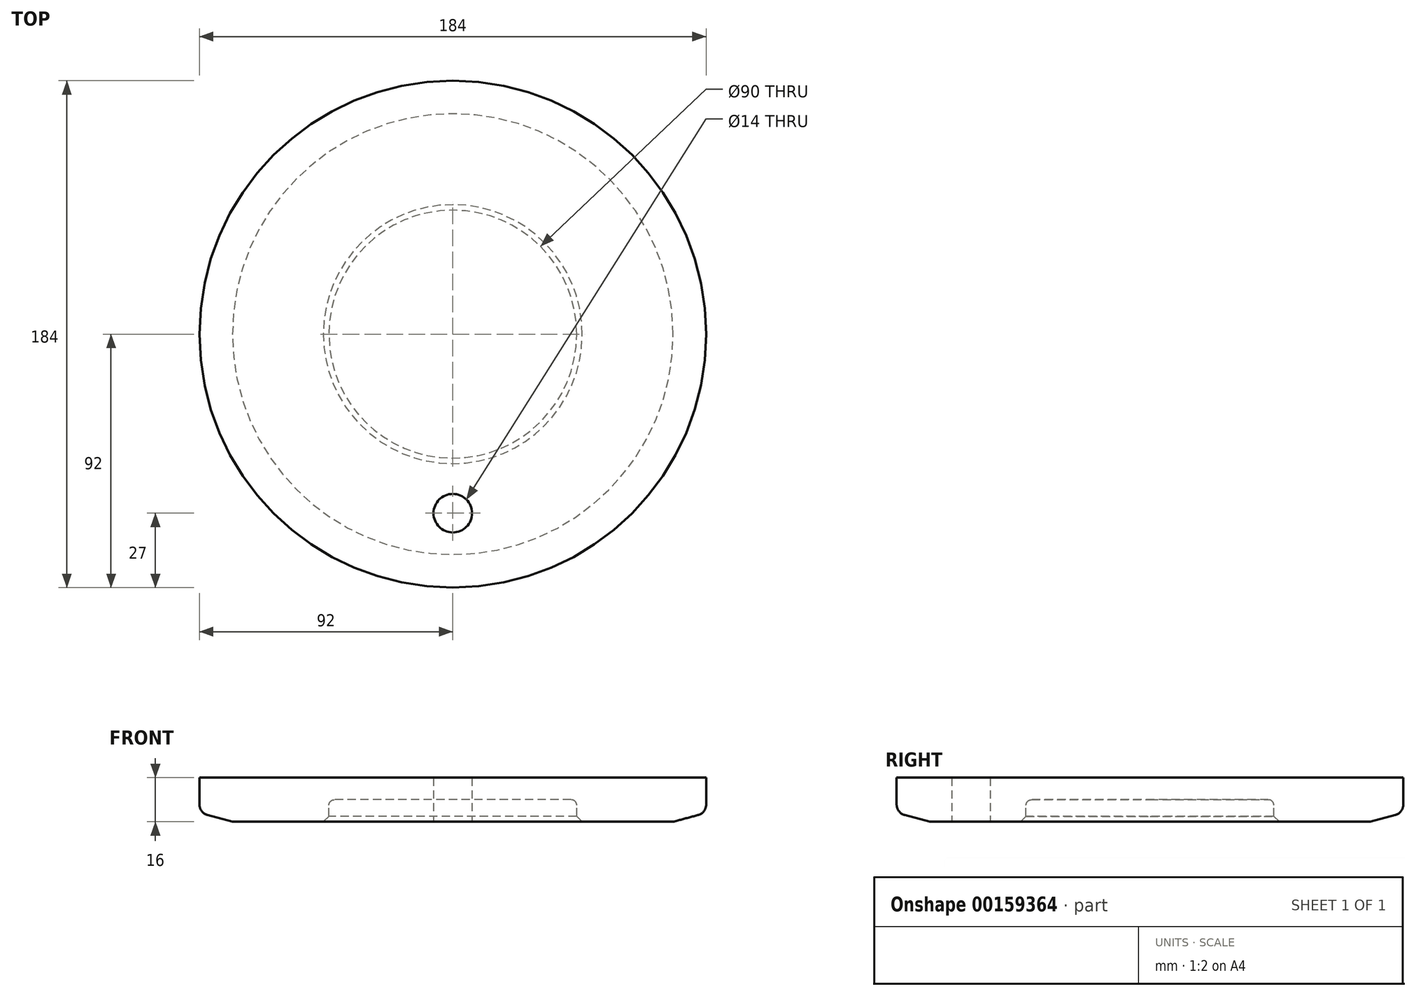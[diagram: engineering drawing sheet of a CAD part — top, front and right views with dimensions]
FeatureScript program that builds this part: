
annotation { "Feature Type Name" : "Feature", "Feature Type Description" : "" }
export const myFeature = defineFeature(function(context is Context, id is Id, definition is map)
    precondition{}
    {
        {
            var Q0;
            Q0=qCreatedBy(makeId("Right.planeOp"),FACE);
            var sketch = newSketch(context, id + "F0", { "sketchPlane" : qUnion([Q0])});
            skLineSegment(sketch, "E0", {"start": v(-50.07, 0) * mm, "end": v(57.08, 0) * mm, "construction": true});
            skLineSegment(sketch, "E1", {"start": v(0, 48.61) * mm, "end": v(0, -46.86) * mm, "construction": true});
            skLineSegment(sketch, "E2.bottom", {"start": v(0, 16) * mm, "end": v(92, 16) * mm});
            skLineSegment(sketch, "E2.top", {"start": v(45, 0) * mm, "end": v(80, 0) * mm});
            skLineSegment(sketch, "E2.left", {"start": v(0, 16) * mm, "end": v(0, 0) * mm});
            skLineSegment(sketch, "E2.right", {"start": v(92, 16) * mm, "end": v(92, 6.28) * mm});
            skPoint(sketch, "E3", {"position": v(80, 0) * mm});
            skLineSegment(sketch, "E4", {"start": v(80, 0) * mm, "end": v(89.04, 2.42) * mm});
            skPoint(sketch, "E5.visualSharp", {"position": v(92, 3.22) * mm});
            skArc(sketch, "E5.filletArc", {"start": v(89.04, 2.42) * mm, "mid": v(91.17, 3.85) * mm, "end": v(92, 6.28) * mm});
            skPoint(sketch, "E6", {"position": v(45, 0) * mm});
            skLineSegment(sketch, "E7.top", {"start": v(43, 8) * mm, "end": v(0, 8) * mm});
            skLineSegment(sketch, "E7.left", {"start": v(45, 0) * mm, "end": v(45, 6) * mm});
            skPoint(sketch, "E8.visualSharp", {"position": v(45, 8) * mm});
            skArc(sketch, "E8.filletArc", {"start": v(45, 6) * mm, "mid": v(44.41, 7.41) * mm, "end": v(43, 8) * mm});
            skSolve(sketch);
        }
        {
            var Q0;
            {var subQ1=sQuery(id+"F0.wireOp",EDGE,"E2.bottom");Q0=makeQuery(id+"F0.imprint","IMPRINT",FACE,{"disambiguationData":[TD([[makeQuery(id+"F0.imprint","IMPRINT",EDGE,{"derivedFrom":subQ1}),-1.0]])]});}
            var Q1;
            Q1=sQuery(id+"F0.wireOp",EDGE,"E1");
            revolve(context, id + "F1", {"entities" : qUnion([Q0]), "axis" : qUnion([Q1]), "revolveType" : RevolveType.FULL});
        }
        {
            var Q0;
            Q0=makeQuery(id+"F1.opRevolve","SWEPT_EDGE",EDGE,{"disambiguationData":[OSD([sQuery(id+"F0.wireOp",EDGE,"E2.top"),sQuery(id+"F0.wireOp",EDGE,"E7.left")])]});
            chamfer(context, id + "F2", {"entities" : qUnion([Q0]), "chamferType" : ChamferType.OFFSET_ANGLE, "width" : 2 * mm, "oppositeDirection" : false, "angle" : 45 * degree, "tangentPropagation" : true});
        }
        {
            var Q0;
            Q0=makeQuery(id+"F1.opRevolve","SWEPT_FACE",FACE,{"disambiguationData":[OSD([sQuery(id+"F0.wireOp",EDGE,"E2.top")])]});
            var sketch = newSketch(context, id + "F3", { "sketchPlane" : qUnion([Q0])});
            skCircle(sketch, "E9", {"center": v(0, 0) * mm, "radius": 65 * mm, "construction": true});
            skPoint(sketch, "E10", {"position": v(0, 65) * mm});
            skCircle(sketch, "E11", {"center": v(0, 65) * mm, "radius": 7 * mm});
            skSolve(sketch);
        }
        {
            var Q0;
            Q0=makeQuery(id+"F3.imprint","IMPRINT",FACE,{"disambiguationData":[TD([[makeQuery(id+"F3.imprint","IMPRINT",EDGE,{"derivedFrom":sQuery(id+"F3.wireOp",EDGE,"E11")}),1.0]])]});
            extrude(context, id + "F4", {"entities" : qUnion([Q0]), "operationType" : NewBodyOperationType.REMOVE, "oppositeDirection" : true, "depth" : 25 * mm});
        }
        {
            var Q0;
            Q0=qCreatedBy(makeId("Front.planeOp"),FACE);
            var sketch = newSketch(context, id + "F5", { "sketchPlane" : qUnion([Q0])});
            skLineSegment(sketch, "E12", {"start": v(0, -70.02) * mm, "end": v(0, 73.73) * mm, "construction": true});
            skSolve(sketch);
        }
    });
